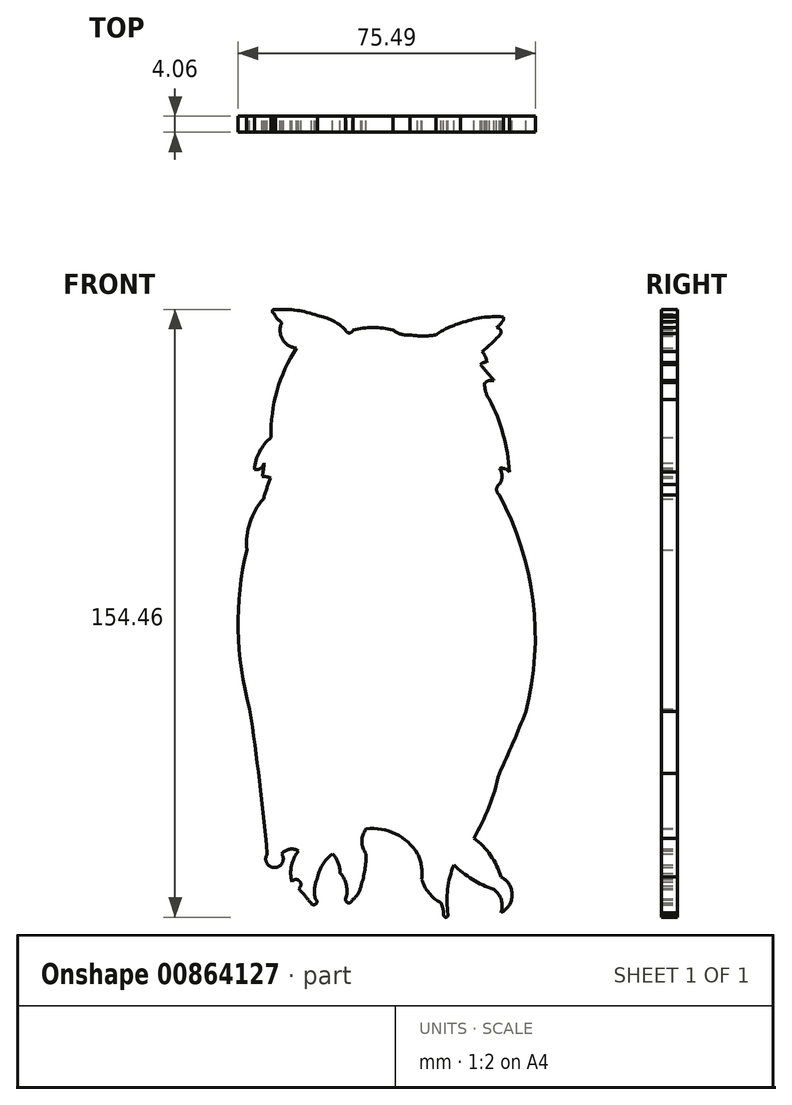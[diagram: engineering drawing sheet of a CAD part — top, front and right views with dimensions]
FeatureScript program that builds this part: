
annotation { "Feature Type Name" : "Feature", "Feature Type Description" : "" }
export const myFeature = defineFeature(function(context is Context, id is Id, definition is map)
    precondition{}
    {
        {
            var Q0;
            Q0=qCreatedBy(makeId("Front.planeOp"),FACE);
            var sketch = newSketch(context, id + "F0", { "sketchPlane" : qUnion([Q0])});
            skArc(sketch, "E0", {"start": v(-66.8, 76) * mm, "mid": v(-66.02, 74.65) * mm, "end": v(-64.84, 73.62) * mm});
            skArc(sketch, "E1", {"start": v(-64.84, 73.62) * mm, "mid": v(-64.67, 69.4) * mm, "end": v(-61.1, 67.14) * mm});
            skArc(sketch, "E2", {"start": v(-61.1, 67.14) * mm, "mid": v(-66.06, 56.3) * mm, "end": v(-67.57, 44.48) * mm});
            skArc(sketch, "E3", {"start": v(-67.57, 44.48) * mm, "mid": v(-70.5, 40.8) * mm, "end": v(-71.83, 36.3) * mm});
            skArc(sketch, "E4", {"start": v(-71.83, 36.3) * mm, "mid": v(-70.24, 36.59) * mm, "end": v(-69.31, 37.92) * mm});
            skPoint(sketch, "E5.orphan", {"position": v(-69.27, 36.3) * mm});
            skArc(sketch, "E6", {"start": v(-69.8, 34.5) * mm, "mid": v(-69.52, 36.2) * mm, "end": v(-69.31, 37.92) * mm});
            skArc(sketch, "E7", {"start": v(-67.7, 34.2) * mm, "mid": v(-68.74, 34.45) * mm, "end": v(-69.8, 34.5) * mm});
            skArc(sketch, "E8", {"start": v(-67.7, 34.2) * mm, "mid": v(-68.64, 31.54) * mm, "end": v(-69.5, 28.84) * mm});
            skArc(sketch, "E9", {"start": v(-69.5, 28.84) * mm, "mid": v(-72.95, 22.82) * mm, "end": v(-73.74, 15.92) * mm});
            skArc(sketch, "E10", {"start": v(-73.74, 15.92) * mm, "mid": v(-75.91, -4.32) * mm, "end": v(-72.98, -24.47) * mm});
            skArc(sketch, "E11", {"start": v(-68.53, -61.33) * mm, "mid": v(-70.52, -42.87) * mm, "end": v(-72.98, -24.47) * mm});
            skArc(sketch, "E12", {"start": v(-68.53, -61.33) * mm, "mid": v(-66.69, -64.84) * mm, "end": v(-64.85, -61.33) * mm});
            skArc(sketch, "E13", {"start": v(-60.58, -60.6) * mm, "mid": v(-62.85, -60.16) * mm, "end": v(-64.85, -61.33) * mm});
            skArc(sketch, "E14", {"start": v(-60.58, -60.6) * mm, "mid": v(-62.37, -64.33) * mm, "end": v(-62.3, -68.48) * mm});
            skArc(sketch, "E15", {"start": v(-57.35, -73.96) * mm, "mid": v(-58.92, -72.03) * mm, "end": v(-60.58, -70.18) * mm});
            skArc(sketch, "E16", {"start": v(-55.88, -67.77) * mm, "mid": v(-56.53, -70.27) * mm, "end": v(-56.29, -72.84) * mm});
            skPoint(sketch, "E16.startSnap0", {"position": v(-59.9, -67.77) * mm});
            skArc(sketch, "E17", {"start": v(-51.92, -61.33) * mm, "mid": v(-54.52, -64.17) * mm, "end": v(-55.88, -67.77) * mm});
            skArc(sketch, "E18", {"start": v(-50, -66.25) * mm, "mid": v(-50.52, -63.62) * mm, "end": v(-51.92, -61.33) * mm});
            skArc(sketch, "E19", {"start": v(-48.6, -72.84) * mm, "mid": v(-48.41, -69.35) * mm, "end": v(-50, -66.25) * mm});
            skArc(sketch, "E20", {"start": v(-46.99, -73.1) * mm, "mid": v(-45.49, -71.53) * mm, "end": v(-44.72, -69.5) * mm});
            skArc(sketch, "E21", {"start": v(-44.72, -69.5) * mm, "mid": v(-43.72, -65.47) * mm, "end": v(-43.4, -61.33) * mm});
            skArc(sketch, "E22", {"start": v(-43.4, -55) * mm, "mid": v(-44.51, -58.17) * mm, "end": v(-43.4, -61.33) * mm});
            skArc(sketch, "E23", {"start": v(-30.32, -61.33) * mm, "mid": v(-35.94, -56.27) * mm, "end": v(-43.4, -55) * mm});
            skArc(sketch, "E24", {"start": v(-29.29, -67.77) * mm, "mid": v(-29.36, -64.48) * mm, "end": v(-30.32, -61.33) * mm});
            skArc(sketch, "E25", {"start": v(-29.29, -67.77) * mm, "mid": v(-27.45, -71.32) * mm, "end": v(-24.35, -73.85) * mm});
            skArc(sketch, "E26", {"start": v(-23.7, -76.9) * mm, "mid": v(-23.89, -75.34) * mm, "end": v(-24.35, -73.85) * mm});
            skLineSegment(sketch, "E27", {"start": v(-23.7, -76.9) * mm, "end": v(-23.7, -76.9) * mm});
            skArc(sketch, "E28", {"start": v(-9.16, -76.31) * mm, "mid": v(-6.33, -71.76) * mm, "end": v(-9.16, -67.2) * mm});
            skArc(sketch, "E29", {"start": v(-9.16, -67.2) * mm, "mid": v(-11.8, -61.73) * mm, "end": v(-16.06, -57.38) * mm});
            skArc(sketch, "E30", {"start": v(-16.06, -57.38) * mm, "mid": v(-12.2, -49.39) * mm, "end": v(-9.6, -40.9) * mm});
            skArc(sketch, "E31", {"start": v(-9.6, -40.9) * mm, "mid": v(-6.08, -33.1) * mm, "end": v(-2.84, -25.18) * mm});
            skArc(sketch, "E32", {"start": v(-2.84, -25.18) * mm, "mid": v(-1, 2.98) * mm, "end": v(-9.6, 29.85) * mm});
            skArc(sketch, "E33", {"start": v(-9.6, 32.56) * mm, "mid": v(-10.26, 31.2) * mm, "end": v(-9.6, 29.85) * mm});
            skArc(sketch, "E34", {"start": v(-9.6, 32.56) * mm, "mid": v(-8.92, 34.57) * mm, "end": v(-9.6, 36.58) * mm});
            skArc(sketch, "E35", {"start": v(-7.02, 35.7) * mm, "mid": v(-8.19, 36.5) * mm, "end": v(-9.6, 36.58) * mm});
            skArc(sketch, "E36", {"start": v(-7.02, 35.7) * mm, "mid": v(-8.6, 45.19) * mm, "end": v(-12.1, 54.14) * mm});
            skArc(sketch, "E37", {"start": v(-13.28, 58.37) * mm, "mid": v(-13.07, 56.15) * mm, "end": v(-12.1, 54.14) * mm});
            skArc(sketch, "E38", {"start": v(-10.9, 58.88) * mm, "mid": v(-12.15, 58.9) * mm, "end": v(-13.28, 58.37) * mm});
            skArc(sketch, "E39", {"start": v(-14.35, 62.96) * mm, "mid": v(-12.66, 60.89) * mm, "end": v(-10.9, 58.88) * mm});
            skArc(sketch, "E40", {"start": v(-12.73, 63.55) * mm, "mid": v(-13.62, 63.47) * mm, "end": v(-14.35, 62.96) * mm});
            skArc(sketch, "E41", {"start": v(-12.73, 63.55) * mm, "mid": v(-13.16, 65.02) * mm, "end": v(-13.94, 66.34) * mm});
            skArc(sketch, "E42", {"start": v(-13.94, 66.34) * mm, "mid": v(-11.4, 68.47) * mm, "end": v(-9.15, 70.9) * mm});
            skArc(sketch, "E43", {"start": v(-9.15, 70.9) * mm, "mid": v(-9.38, 71.9) * mm, "end": v(-10.3, 72.37) * mm});
            skArc(sketch, "E44", {"start": v(-10.3, 72.37) * mm, "mid": v(-9.49, 73.02) * mm, "end": v(-8.86, 73.84) * mm});
            skArc(sketch, "E45", {"start": v(-8.86, 73.84) * mm, "mid": v(-8.52, 74.4) * mm, "end": v(-8.53, 75.06) * mm});
            skArc(sketch, "E46", {"start": v(-8.53, 75.06) * mm, "mid": v(-14.06, 74.88) * mm, "end": v(-19.4, 73.48) * mm});
            skArc(sketch, "E47", {"start": v(-19.4, 73.48) * mm, "mid": v(-22.7, 72.25) * mm, "end": v(-25.72, 70.46) * mm});
            skArc(sketch, "E48", {"start": v(-32.23, 70.46) * mm, "mid": v(-28.98, 70.24) * mm, "end": v(-25.72, 70.46) * mm});
            skArc(sketch, "E49", {"start": v(-36.62, 71.74) * mm, "mid": v(-34.55, 70.7) * mm, "end": v(-32.23, 70.46) * mm});
            skArc(sketch, "E50", {"start": v(-36.62, 71.74) * mm, "mid": v(-41.66, 72.35) * mm, "end": v(-46.7, 71.74) * mm});
            skArc(sketch, "E51", {"start": v(-48.67, 71.74) * mm, "mid": v(-47.68, 71.02) * mm, "end": v(-46.7, 71.74) * mm});
            skArc(sketch, "E52", {"start": v(-48.67, 71.74) * mm, "mid": v(-51.94, 74.14) * mm, "end": v(-55.8, 75.4) * mm});
            skArc(sketch, "E53", {"start": v(-55.8, 75.4) * mm, "mid": v(-61.03, 76.74) * mm, "end": v(-66.42, 76.91) * mm});
            skArc(sketch, "E54", {"start": v(-66.42, 76.91) * mm, "mid": v(-67.17, 76.7) * mm, "end": v(-66.8, 76) * mm});
            skPoint(sketch, "E55.center.orphan", {"position": v(-11.59, -57.38) * mm});
            skPoint(sketch, "E56.end.orphan", {"position": v(-23.7, -62.22) * mm});
            skArc(sketch, "E57", {"start": v(-9.16, -76.31) * mm, "mid": v(-9.08, -73.06) * mm, "end": v(-10.95, -70.4) * mm});
            skArc(sketch, "E58", {"start": v(-21.15, -64.1) * mm, "mid": v(-16.4, -67.83) * mm, "end": v(-10.95, -70.4) * mm});
            skArc(sketch, "E59", {"start": v(-21.15, -64.1) * mm, "mid": v(-22.7, -70.34) * mm, "end": v(-22.63, -76.77) * mm});
            skArc(sketch, "E60", {"start": v(-23.7, -76.9) * mm, "mid": v(-23.1, -77.45) * mm, "end": v(-22.63, -76.77) * mm});
            skPoint(sketch, "E61.start.orphan", {"position": v(-55.88, -73.96) * mm});
            skArc(sketch, "E62", {"start": v(-57.35, -73.96) * mm, "mid": v(-56.15, -74.04) * mm, "end": v(-56.29, -72.84) * mm});
            skArc(sketch, "E63", {"start": v(-60.58, -70.18) * mm, "mid": v(-60.35, -68.23) * mm, "end": v(-62.3, -68.48) * mm});
            skArc(sketch, "E64", {"start": v(-48.6, -72.84) * mm, "mid": v(-47.92, -73.8) * mm, "end": v(-46.99, -73.1) * mm});
            skPoint(sketch, "E65.orphan", {"position": v(-49.08, -73.96) * mm});
            skPoint(sketch, "E66.orphan", {"position": v(-69.27, 38.17) * mm});
            skSolve(sketch);
        }
        {
            var Q0;
            Q0 = qSketchRegion(id + "F0", true);
            extrude(context, id + "F1", {"entities" : qUnion([Q0]), "depth" : 4.06 * mm, "offsetDistance" : 25.4 * mm});
        }
    });
